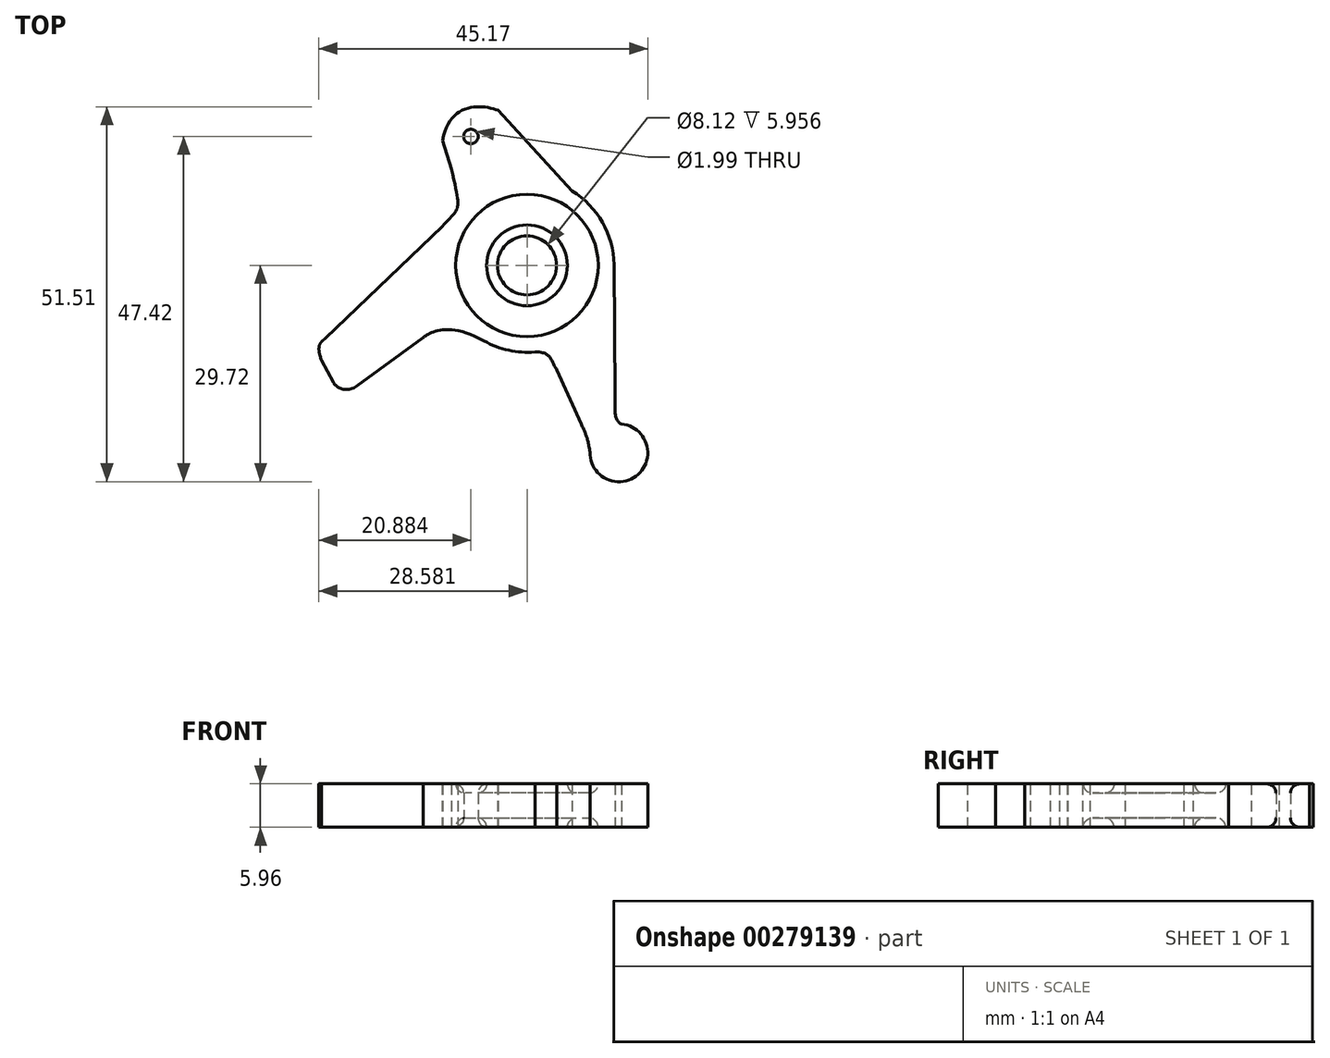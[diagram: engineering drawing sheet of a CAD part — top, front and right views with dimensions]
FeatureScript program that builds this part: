
annotation { "Feature Type Name" : "Feature", "Feature Type Description" : "" }
export const myFeature = defineFeature(function(context is Context, id is Id, definition is map)
    precondition{}
    {
        {
            var Q0;
            Q0=qCreatedBy(makeId("Top.planeOp"),FACE);
            var sketch = newSketch(context, id + "F0", { "sketchPlane" : qUnion([Q0])});
            skCircle(sketch, "E0", {"center": v(-19.38, -23.38) * mm, "radius": 4.06 * mm});
            skArc(sketch, "E1", {"start": v(-25.3, -33.75) * mm, "mid": v(-21.92, -35.05) * mm, "end": v(-18.3, -35.27) * mm});
            skCircle(sketch, "E2", {"center": v(-27.08, -5.68) * mm, "radius": 1 * mm});
            skArc(sketch, "E3", {"start": v(-10.73, -49.04) * mm, "mid": v(-4.12, -52.09) * mm, "end": v(-6.41, -45.18) * mm});
            skLineSegment(sketch, "E4", {"start": v(-7.44, -23.28) * mm, "end": v(-7.3, -41.22) * mm});
            skLineSegment(sketch, "E5", {"start": v(-15.26, -37.72) * mm, "end": v(-11.91, -45.2) * mm});
            skLineSegment(sketch, "E6", {"start": v(-29.78, -10.1) * mm, "end": v(-30.95, -6.23) * mm});
            skLineSegment(sketch, "E7", {"start": v(-13.21, -13.16) * mm, "end": v(-23.37, -2.08) * mm});
            skFitSpline(sketch, "E8", {"points": [v(-30.95, -6.23) * mm, v(-23.37, -2.08) * mm], "startDerivative": vector(2.5, 15.8) * mm, "endDerivative": vector(6.78, -2.67) * mm});
            skLineSegment(sketch, "E9", {"start": v(-47.71, -34.01) * mm, "end": v(-31.03, -18.05) * mm});
            skLineSegment(sketch, "E10", {"start": v(-42.78, -39.94) * mm, "end": v(-33.63, -33.27) * mm});
            skFitSpline(sketch, "E11", {"points": [v(-33.63, -33.27) * mm, v(-25.3, -33.75) * mm], "startDerivative": vector(1.88, 1.31) * mm, "endDerivative": vector(15.2, -8.6) * mm});
            skLineSegment(sketch, "E12", {"start": v(-47.58, -36.44) * mm, "end": v(-45.98, -39.47) * mm});
            skFitSpline(sketch, "E13", {"points": [v(-47.03, -33.36) * mm, v(-47.58, -36.44) * mm], "startDerivative": vector(-1.65, -1.58) * mm, "endDerivative": vector(2.69, -6.75) * mm});
            skFitSpline(sketch, "E14", {"points": [v(-45.98, -39.47) * mm, v(-42.78, -39.94) * mm], "startDerivative": vector(0.75, -1.41) * mm, "endDerivative": vector(4.75, 3.46) * mm});
            skPoint(sketch, "E15.orphan", {"position": v(-48.47, -34.74) * mm});
            skArc(sketch, "E16.trimOffspring", {"start": v(-7.44, -23.28) * mm, "mid": v(-9, -17.47) * mm, "end": v(-13.21, -13.16) * mm});
            skFitSpline(sketch, "E17", {"points": [v(-29.78, -10.1) * mm, v(-31.03, -18.05) * mm], "startDerivative": vector(4.5, -18.96) * mm, "endDerivative": vector(-7.25, -8.19) * mm});
            skPoint(sketch, "E18.orphan", {"position": v(-28.18, -15.32) * mm});
            skFitSpline(sketch, "E19", {"points": [v(-18.3, -35.27) * mm, v(-15.26, -37.72) * mm], "startDerivative": vector(7.38, 0.09) * mm, "endDerivative": vector(2.89, -3.6) * mm});
            skFitSpline(sketch, "E20", {"points": [v(-6.41, -45.18) * mm, v(-7.3, -41.22) * mm], "startDerivative": vector(-3.8, 1.92) * mm, "endDerivative": vector(-0.4, 3.89) * mm});
            skFitSpline(sketch, "E21", {"points": [v(-10.73, -49.04) * mm, v(-11.91, -45.2) * mm], "startDerivative": vector(-0.82, 5.43) * mm, "endDerivative": vector(-1.83, 4.09) * mm});
            skPoint(sketch, "E22.orphan", {"position": v(-7.26, -45.2) * mm});
            skSolve(sketch);
        }
        {
            var Q0;
            Q0 = qSketchRegion(id + "F0", true);
            extrude(context, id + "F1", {"entities" : qUnion([Q0]), "depth" : 5.96 * mm});
        }
        {
            var Q0;
            Q0=makeQuery(id+"F1.opExtrude","CAP_FACE",FACE,{"disambiguationData":[OSD([sQuery(id+"F0.wireOp",EDGE,"E0"),sQuery(id+"F0.wireOp",EDGE,"E1"),sQuery(id+"F0.wireOp",EDGE,"E2"),sQuery(id+"F0.wireOp",EDGE,"E3"),sQuery(id+"F0.wireOp",EDGE,"E4"),sQuery(id+"F0.wireOp",EDGE,"E5"),sQuery(id+"F0.wireOp",EDGE,"E6"),sQuery(id+"F0.wireOp",EDGE,"E7"),sQuery(id+"F0.wireOp",EDGE,"E8"),sQuery(id+"F0.wireOp",EDGE,"E9"),sQuery(id+"F0.wireOp",EDGE,"E10"),sQuery(id+"F0.wireOp",EDGE,"E11"),sQuery(id+"F0.wireOp",EDGE,"E12"),sQuery(id+"F0.wireOp",EDGE,"E13"),sQuery(id+"F0.wireOp",EDGE,"E14"),sQuery(id+"F0.wireOp",EDGE,"E16.trimOffspring"),sQuery(id+"F0.wireOp",EDGE,"E17"),sQuery(id+"F0.wireOp",EDGE,"E19"),sQuery(id+"F0.wireOp",EDGE,"E20"),sQuery(id+"F0.wireOp",EDGE,"E21")])],"isStart":false});
            var sketch = newSketch(context, id + "F2", { "sketchPlane" : qUnion([Q0])});
            skCircle(sketch, "E23", {"center": v(-19.38, -23.38) * mm, "radius": 5.55 * mm});
            skCircle(sketch, "E24", {"center": v(-19.38, -23.38) * mm, "radius": 9.78 * mm});
            skSolve(sketch);
        }
        {
            var Q0;
            Q0 = qSketchRegion(id + "F2", true);
            extrude(context, id + "F3", {"entities" : qUnion([Q0]), "operationType" : NewBodyOperationType.REMOVE, "oppositeDirection" : true, "depth" : 1.27 * mm});
        }
        {
            var Q0;
            Q0=makeQuery(id+"F3.boolean.opBoolean","COPY",EDGE,{"derivedFrom":makeQuery(id+"F3.opExtrude","CAP_EDGE",EDGE,{"disambiguationData":[OSD([sQuery(id+"F2.wireOp",EDGE,"E24")])],"isStart":false})});
            var Q1;
            Q1=makeQuery(id+"F3.boolean.opBoolean","COPY",EDGE,{"derivedFrom":makeQuery(id+"F3.opExtrude","CAP_EDGE",EDGE,{"disambiguationData":[OSD([sQuery(id+"F2.wireOp",EDGE,"E23")])],"isStart":false})});
            fillet(context, id + "F4", {"entities" : qUnion([Q0, Q1]), "radius" : 1.27 * mm, "tangentPropagation" : true, "allowEdgeOverflow" : false});
        }
        {
            var Q0;
            Q0=makeQuery(id+"F1.opExtrude","CAP_EDGE",EDGE,{"disambiguationData":[OSD([sQuery(id+"F0.wireOp",EDGE,"E2")])],"isStart":false});
            var Q1;
            Q1=makeQuery(id+"F1.opExtrude","CAP_EDGE",EDGE,{"disambiguationData":[OSD([sQuery(id+"F0.wireOp",EDGE,"E2")])],"isStart":true});
            fillet(context, id + "F5", {"entities" : qUnion([Q0, Q1]), "radius" : 1.27 * mm, "tangentPropagation" : true, "allowEdgeOverflow" : false});
        }
        {
            var Q0;
            Q0=makeQuery(id+"F1.opExtrude","CAP_FACE",FACE,{"disambiguationData":[OSD([sQuery(id+"F0.wireOp",EDGE,"E0"),sQuery(id+"F0.wireOp",EDGE,"E1"),sQuery(id+"F0.wireOp",EDGE,"E2"),sQuery(id+"F0.wireOp",EDGE,"E3"),sQuery(id+"F0.wireOp",EDGE,"E4"),sQuery(id+"F0.wireOp",EDGE,"E5"),sQuery(id+"F0.wireOp",EDGE,"E6"),sQuery(id+"F0.wireOp",EDGE,"E7"),sQuery(id+"F0.wireOp",EDGE,"E8"),sQuery(id+"F0.wireOp",EDGE,"E9"),sQuery(id+"F0.wireOp",EDGE,"E10"),sQuery(id+"F0.wireOp",EDGE,"E11"),sQuery(id+"F0.wireOp",EDGE,"E12"),sQuery(id+"F0.wireOp",EDGE,"E13"),sQuery(id+"F0.wireOp",EDGE,"E14"),sQuery(id+"F0.wireOp",EDGE,"E16.trimOffspring"),sQuery(id+"F0.wireOp",EDGE,"E17"),sQuery(id+"F0.wireOp",EDGE,"E19"),sQuery(id+"F0.wireOp",EDGE,"E20"),sQuery(id+"F0.wireOp",EDGE,"E21")])],"isStart":true});
            var sketch = newSketch(context, id + "F6", { "sketchPlane" : qUnion([Q0])});
            skCircle(sketch, "E25", {"center": v(-19.38, 23.38) * mm, "radius": 5.55 * mm});
            skCircle(sketch, "E26", {"center": v(-19.38, 23.38) * mm, "radius": 9.78 * mm});
            skSolve(sketch);
        }
        {
            var Q0;
            Q0 = qSketchRegion(id + "F6", true);
            extrude(context, id + "F7", {"entities" : qUnion([Q0]), "operationType" : NewBodyOperationType.REMOVE, "oppositeDirection" : true, "depth" : 1.27 * mm});
        }
        {
            var Q0;
            Q0=makeQuery(id+"F7.boolean.opBoolean","COPY",EDGE,{"derivedFrom":makeQuery(id+"F7.opExtrude","CAP_EDGE",EDGE,{"disambiguationData":[OSD([sQuery(id+"F6.wireOp",EDGE,"E26")])],"isStart":false})});
            var Q1;
            Q1=makeQuery(id+"F7.boolean.opBoolean","COPY",EDGE,{"derivedFrom":makeQuery(id+"F7.opExtrude","CAP_EDGE",EDGE,{"disambiguationData":[OSD([sQuery(id+"F6.wireOp",EDGE,"E25")])],"isStart":false})});
            fillet(context, id + "F8", {"entities" : qUnion([Q0, Q1]), "radius" : 1.27 * mm, "tangentPropagation" : true, "allowEdgeOverflow" : false});
        }
    });
